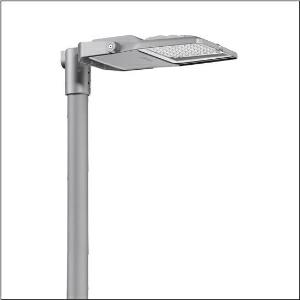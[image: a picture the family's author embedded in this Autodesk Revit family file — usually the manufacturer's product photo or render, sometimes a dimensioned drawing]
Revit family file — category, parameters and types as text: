
# Revit family: floodlight_fl_21_iq_mini___pl43_5xa7772c2a3a_c494
name_source: partatom
category: Lighting Fixtures
units: mm (PartAtom-declared; Revit-internal decimal feet)

## family parameters
Cut with Voids When Loaded = No
Host = Face
Light Source = No
Part Type = Normal
Room Calculation Point = No
Round Connector Dimension = Use Diameter
Shared = No

## types (1)
- --- (1 x LED, 12520 lm, 87.2 W, 3000K)
    Apparent Load = 87 VA
    CIE Flux Codes = 27 78 99 100 100
    Color Rendering = 70
    Color Temperature = 3000K
    Default Elevation = 1800 mm
    Description = Floodlight FL 21 iQ mini, floodlight, primary light control with lens, of PMMA, primary optical cover: protective disc, of toughened safety glass, transparent, light distribution: PL43, light emission: direct distribution, installation type: surface-mounted, lamps: LED, High Power LED, rated values: 12.520lm | 87,2W | 143,6lm/W (begin service life); end service life: 12.520lm | 92,1W; at 50% lumin. flux: 6.260lm | 40,1W | 156,1lm/W, colour temperature: 3000K, colour rendering: CRI > 70, light colour: 730, light setting 1 begin service life: 100% | 12.520lm | 87,2W | 143,6lm/W | 3.000K, light setting 1 end service life: 92,1W, further light settings possible, control: pre-setting: linear dimming characteristic, Auto-Match, Temp-Guard, Night-Set, Smart-Wire, Desk-Remote (wireless, voltage-free reading and setting of iQ features in the workshop via application-optimized NFC function/RFID function), optimised constant luminous flux control (CLO 2.0), Light-Fading, Lumen-Switch, with terminal, 6-pole, mains connection: 220..240V, AC, 50/60Hz, luminaire housing, of diecast aluminium, powder-coated, SITECO metallic grey (DB 702S), corrosivity category C5 mid according to DIN EN ISO 12944suitable for swimming poolschlorine-resistant, sealing non-destructively replaceable, please order mast flange separately, mast bracket, of steel, galvanised, powder-coated, protection rating (complete): IP66, insulation class (complete): insulation class II (safety insulation), certification: CE, ENEC, VDE, protection symbol: D, impact resistance: IK08, permissible operating ambient temperature: -40..+40°C, permissible operating ambient temperature for outdoor applications: -40..+50°C, standard: DIN EN 12944, LABS conformity tested according to VDMA 24364:2018-05, packaging unit: 1 piece

Light Distribution: PL43
    Height = 70 mm
    Lamp = 1 x LED
    Lamp Light Flux = 12520 lm
    Lamp Power = 87.2 W
    Lamp count = 1
    Length = 485 mm
    Luminous efficacy = 144 lm/W
    Manufacturer = Siteco
    ModVariant = No
    Model = 5XA7772C2A3A
    Mounting Place = Pole
    Mounting Type = Pole annexe
    Number of Poles = 1
    OnlyDefault = Yes
    Power Factor = 1
    Product Name = Floodlight FL 21 iQ mini | PL43
    Product group = floodlight | pylon annexe
    ProductGroupID = 6201
    Protection Class = Protection class II
    Protection Degree = IP 66
    RLX_Detail_Level = 1
    RLX_Emergency_Light_Flux = 0 lm
    RLX_Emergency_Type = 0
    RLX_Emergency_Type_DB = No
    RlxData = <blob elided: 101577 chars, md5=564f8453>
    Socket = socket
    Standby Power = 0 W
    System Light Flux = 12520 lm
    System Power = 87 W
    Type Comments = factory setting: luminous flux: 100 % | dim-lin: 254 | 456 mA
    Type Image = l_1007125.jpg
    URL = http://relux.com
    VarID = @adj_163323
    Voltage = 0 V
    Weight = 0.00 kg
    Width = 337 mm

## geometry (parser evidence)
native form markers: Blend x4, Sweep x12
no freeform markers — native parametric forms only
